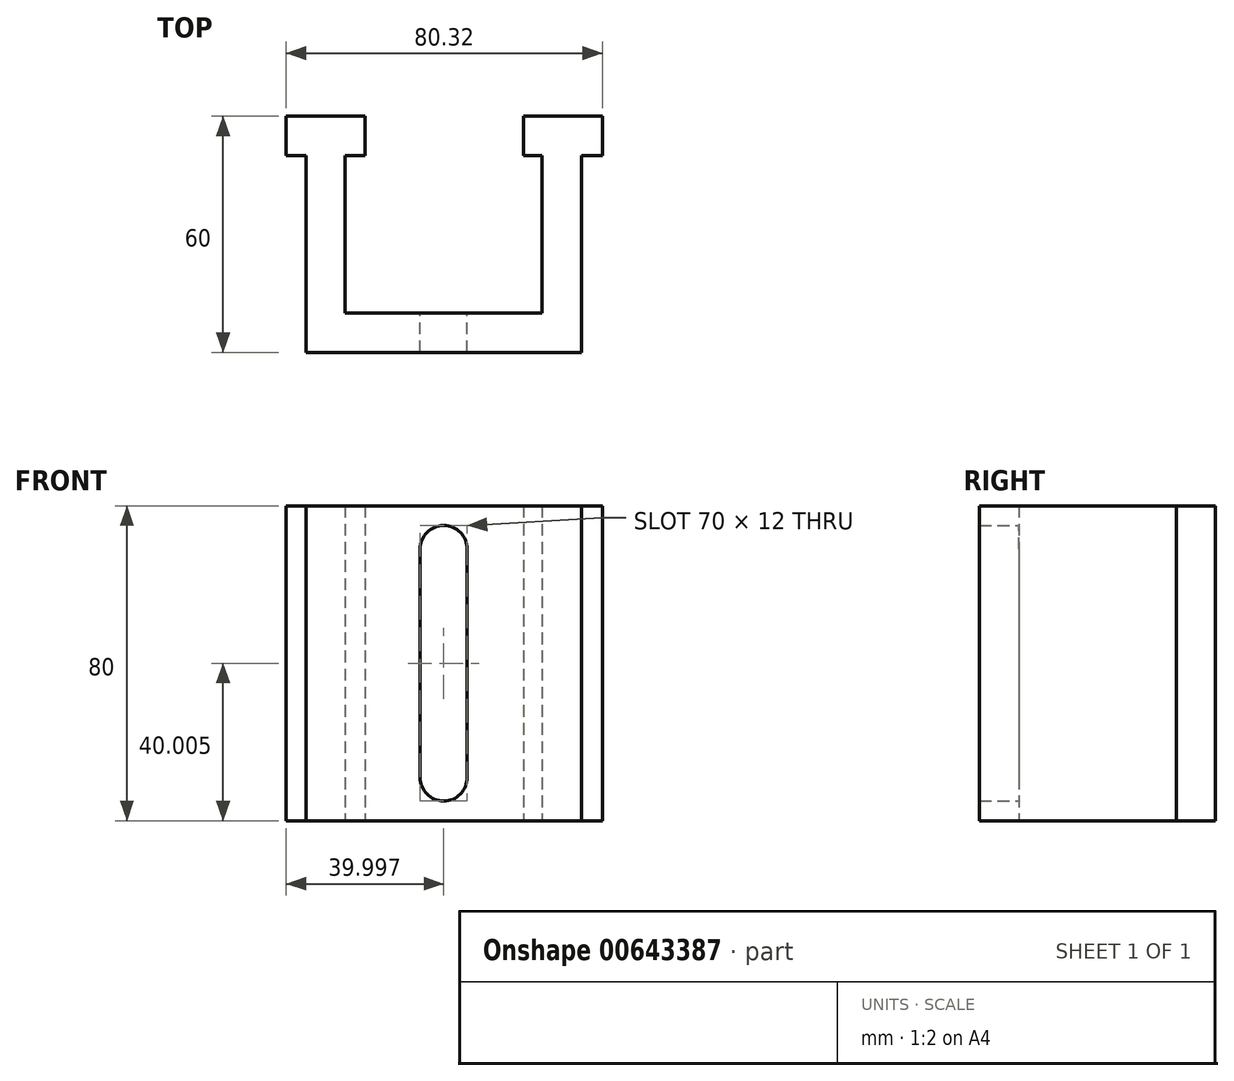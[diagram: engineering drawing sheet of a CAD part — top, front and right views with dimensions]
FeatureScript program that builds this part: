
annotation { "Feature Type Name" : "Feature", "Feature Type Description" : "" }
export const myFeature = defineFeature(function(context is Context, id is Id, definition is map)
    precondition{}
    {
        {
            var Q0;
            Q0=qCreatedBy(makeId("Front.planeOp"),FACE);
            var sketch = newSketch(context, id + "F0", { "sketchPlane" : qUnion([Q0])});
            skLineSegment(sketch, "E0", {"start": v(-34.4, 42.01) * mm, "end": v(-34.4, -37.99) * mm});
            skLineSegment(sketch, "E1", {"start": v(-34.4, 42.01) * mm, "end": v(35.6, 42.01) * mm});
            skLineSegment(sketch, "E2", {"start": v(35.6, 42.01) * mm, "end": v(35.6, -37.99) * mm});
            skLineSegment(sketch, "E3", {"start": v(35.6, -37.99) * mm, "end": v(-34.4, -37.99) * mm});
            skArc(sketch, "E4", {"start": v(6.6, 31.01) * mm, "mid": v(0.6, 37.01) * mm, "end": v(-5.4, 31.01) * mm});
            skArc(sketch, "E5", {"start": v(-5.4, -26.99) * mm, "mid": v(0.6, -32.99) * mm, "end": v(6.6, -26.99) * mm});
            skLineSegment(sketch, "E6", {"start": v(-5.4, 31.01) * mm, "end": v(-5.4, -26.99) * mm});
            skLineSegment(sketch, "E7", {"start": v(6.6, 31.01) * mm, "end": v(6.6, -26.99) * mm});
            skPoint(sketch, "E8.start.orphan", {"position": v(0.6, -37.99) * mm});
            skPoint(sketch, "E9.start.orphan", {"position": v(0.6, 42.01) * mm});
            skSolve(sketch);
        }
        {
            var Q0;
            Q0 = qSketchRegion(id + "F0", true);
            extrude(context, id + "F1", {"entities" : qUnion([Q0]), "depth" : 10 * mm, "offsetDistance" : 25 * mm});
        }
        {
            var Q0;
            Q0=makeQuery(id+"F1.opExtrude","CAP_FACE",FACE,{"disambiguationData":[OSD([sQuery(id+"F0.wireOp",EDGE,"E0"),sQuery(id+"F0.wireOp",EDGE,"E1"),sQuery(id+"F0.wireOp",EDGE,"E2"),sQuery(id+"F0.wireOp",EDGE,"E3"),sQuery(id+"F0.wireOp",EDGE,"E4"),sQuery(id+"F0.wireOp",EDGE,"E5"),sQuery(id+"F0.wireOp",EDGE,"E6"),sQuery(id+"F0.wireOp",EDGE,"E7")])],"isStart":true});
            var sketch = newSketch(context, id + "F2", { "sketchPlane" : qUnion([Q0])});
            skLineSegment(sketch, "E10", {"start": v(-35.6, 42.01) * mm, "end": v(-35.6, -37.99) * mm});
            skLineSegment(sketch, "E11", {"start": v(-25.6, 42.01) * mm, "end": v(-25.6, -37.99) * mm});
            skLineSegment(sketch, "E12", {"start": v(-25.6, -37.99) * mm, "end": v(-35.6, -37.99) * mm});
            skLineSegment(sketch, "E13", {"start": v(-25.6, 42.01) * mm, "end": v(-35.6, 42.01) * mm});
            skLineSegment(sketch, "E14", {"start": v(34.4, 42.01) * mm, "end": v(34.4, -37.99) * mm});
            skLineSegment(sketch, "E15", {"start": v(24.4, 42.01) * mm, "end": v(24.4, -37.99) * mm});
            skLineSegment(sketch, "E16", {"start": v(24.4, -37.99) * mm, "end": v(34.4, -37.99) * mm});
            skLineSegment(sketch, "E17", {"start": v(24.4, 42.01) * mm, "end": v(34.4, 42.01) * mm});
            skSolve(sketch);
        }
        {
            var Q0;
            Q0 = qSketchRegion(id + "F2", true);
            extrude(context, id + "F3", {"entities" : qUnion([Q0]), "operationType" : NewBodyOperationType.ADD, "depth" : 40 * mm, "offsetDistance" : 25 * mm});
        }
        {
            var Q0;
            Q0=makeQuery(id+"F3.opExtrude","CAP_FACE",FACE,{"disambiguationData":[OSD([sQuery(id+"F2.wireOp",EDGE,"E10"),sQuery(id+"F2.wireOp",EDGE,"E11"),sQuery(id+"F2.wireOp",EDGE,"E12"),sQuery(id+"F2.wireOp",EDGE,"E13")])],"isStart":false});
            var sketch = newSketch(context, id + "F4", { "sketchPlane" : qUnion([Q0])});
            skLineSegment(sketch, "E18", {"start": v(-20.93, 42.01) * mm, "end": v(-20.93, -37.99) * mm});
            skLineSegment(sketch, "E19", {"start": v(-20.93, 42.01) * mm, "end": v(-40.93, 42.01) * mm});
            skPoint(sketch, "E19.endSnap0", {"position": v(-30.6, 42.01) * mm});
            skLineSegment(sketch, "E20", {"start": v(-20.93, -37.99) * mm, "end": v(-40.93, -37.99) * mm});
            skLineSegment(sketch, "E21", {"start": v(-40.93, 42.01) * mm, "end": v(-40.93, -37.99) * mm});
            skLineSegment(sketch, "E22", {"start": v(19.4, 42.01) * mm, "end": v(19.4, -37.98) * mm});
            skLineSegment(sketch, "E23", {"start": v(39.4, 42.01) * mm, "end": v(39.4, -37.98) * mm});
            skLineSegment(sketch, "E24", {"start": v(19.4, 42.01) * mm, "end": v(39.4, 42.01) * mm});
            skLineSegment(sketch, "E25", {"start": v(19.4, -37.98) * mm, "end": v(39.4, -37.98) * mm});
            skSolve(sketch);
        }
        {
            var Q0;
            Q0 = qSketchRegion(id + "F4", true);
            extrude(context, id + "F5", {"entities" : qUnion([Q0]), "operationType" : NewBodyOperationType.ADD, "depth" : 10 * mm, "offsetDistance" : 25 * mm});
        }
    });
